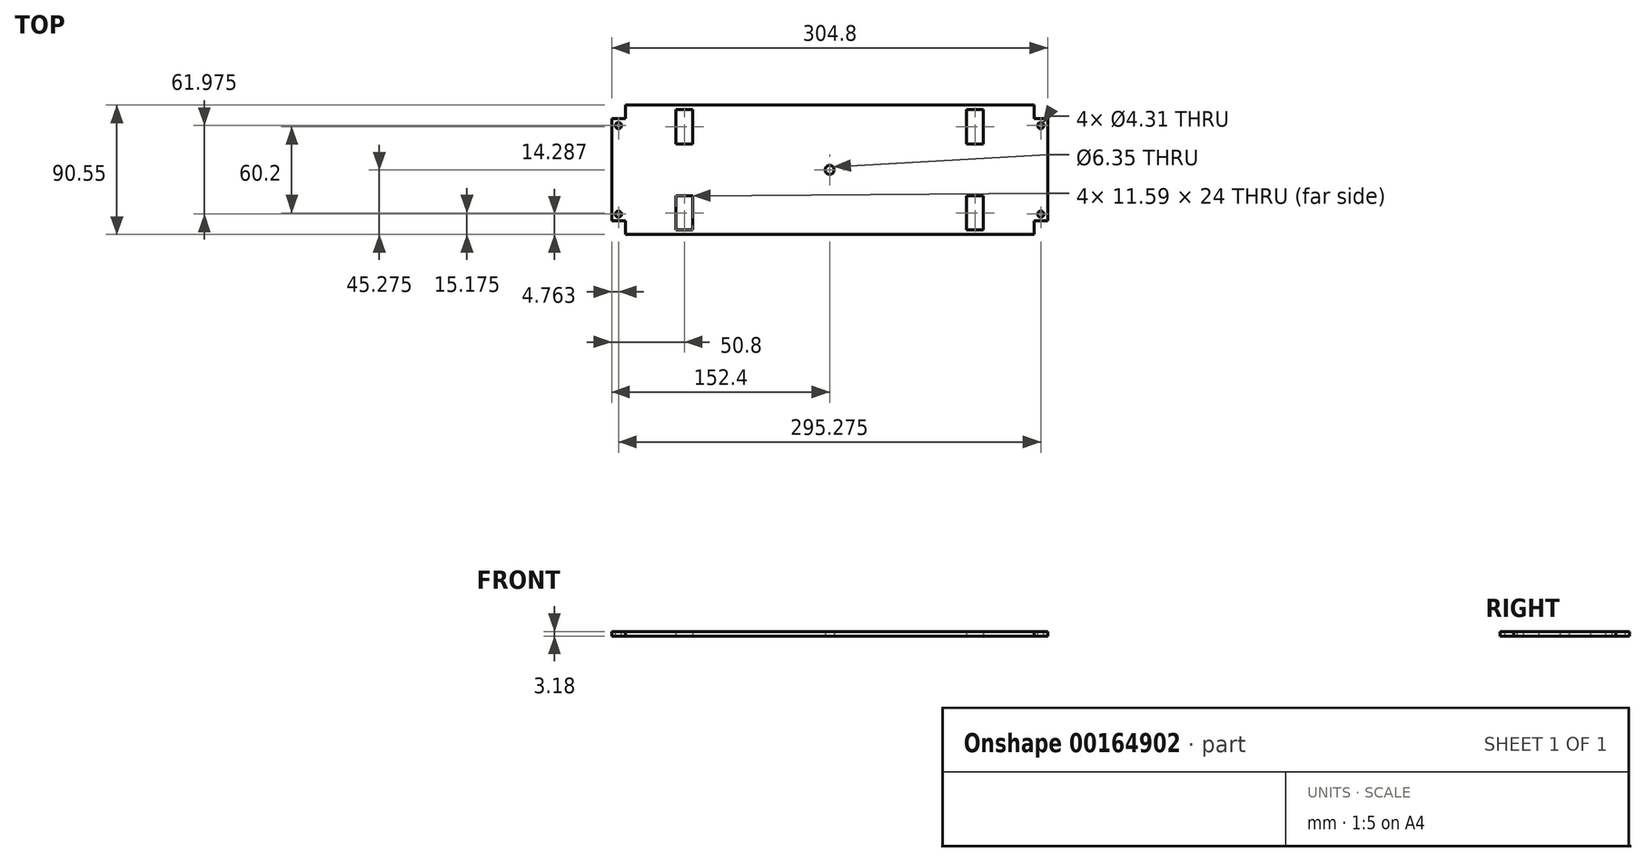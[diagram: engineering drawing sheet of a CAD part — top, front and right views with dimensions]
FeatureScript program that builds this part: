
annotation { "Feature Type Name" : "Feature", "Feature Type Description" : "" }
export const myFeature = defineFeature(function(context is Context, id is Id, definition is map)
    precondition{}
    {
        {
            var Q0;
            Q0=qCreatedBy(makeId("Top.planeOp"),FACE);
            var sketch = newSketch(context, id + "F0", { "sketchPlane" : qUnion([Q0])});
            skLineSegment(sketch, "E0.bottom", {"start": v(0, 0) * mm, "end": v(304.8, 0) * mm});
            skLineSegment(sketch, "E0.top", {"start": v(0, -90.55) * mm, "end": v(304.8, -90.55) * mm});
            skLineSegment(sketch, "E0.left", {"start": v(0, 0) * mm, "end": v(0, -90.55) * mm});
            skLineSegment(sketch, "E0.right", {"start": v(304.8, 0) * mm, "end": v(304.8, -90.55) * mm});
            skLineSegment(sketch, "E1", {"start": v(152.4, 0) * mm, "end": v(152.4, -90.55) * mm, "construction": true});
            skLineSegment(sketch, "E2.bottom", {"start": v(254, -15.18) * mm, "end": v(50.8, -15.18) * mm, "construction": true});
            skLineSegment(sketch, "E2.top", {"start": v(254, -75.38) * mm, "end": v(50.8, -75.38) * mm, "construction": true});
            skLineSegment(sketch, "E2.left", {"start": v(254, -15.18) * mm, "end": v(254, -75.38) * mm, "construction": true});
            skLineSegment(sketch, "E2.right", {"start": v(50.8, -15.18) * mm, "end": v(50.8, -75.38) * mm, "construction": true});
            skPoint(sketch, "E2.middle", {"position": v(152.4, -45.28) * mm});
            skLineSegment(sketch, "E3.bottom", {"start": v(259.8, -3.18) * mm, "end": v(248.2, -3.18) * mm});
            skLineSegment(sketch, "E3.top", {"start": v(259.8, -27.17) * mm, "end": v(248.2, -27.17) * mm});
            skLineSegment(sketch, "E3.left", {"start": v(259.8, -3.18) * mm, "end": v(259.8, -27.18) * mm});
            skLineSegment(sketch, "E3.right", {"start": v(248.2, -3.18) * mm, "end": v(248.2, -27.18) * mm});
            skPoint(sketch, "E3.middle", {"position": v(254, -15.17) * mm});
            skLineSegment(sketch, "E4.bottom", {"start": v(259.8, -87.38) * mm, "end": v(248.2, -87.38) * mm});
            skLineSegment(sketch, "E4.top", {"start": v(259.8, -63.38) * mm, "end": v(248.2, -63.38) * mm});
            skLineSegment(sketch, "E4.left", {"start": v(259.8, -87.38) * mm, "end": v(259.8, -63.38) * mm});
            skLineSegment(sketch, "E4.right", {"start": v(248.2, -87.38) * mm, "end": v(248.2, -63.38) * mm});
            skPoint(sketch, "E4.middle", {"position": v(254, -75.38) * mm});
            skLineSegment(sketch, "E5.bottom", {"start": v(45, -87.38) * mm, "end": v(56.6, -87.38) * mm});
            skLineSegment(sketch, "E5.top", {"start": v(45, -63.38) * mm, "end": v(56.6, -63.38) * mm});
            skLineSegment(sketch, "E5.left", {"start": v(45, -87.38) * mm, "end": v(45, -63.38) * mm});
            skLineSegment(sketch, "E5.right", {"start": v(56.6, -87.38) * mm, "end": v(56.6, -63.38) * mm});
            skPoint(sketch, "E5.middle", {"position": v(50.8, -75.38) * mm});
            skLineSegment(sketch, "E6.bottom", {"start": v(45, -27.18) * mm, "end": v(56.6, -27.18) * mm});
            skLineSegment(sketch, "E6.top", {"start": v(45, -3.17) * mm, "end": v(56.6, -3.17) * mm});
            skLineSegment(sketch, "E6.left", {"start": v(45, -27.18) * mm, "end": v(45, -3.18) * mm});
            skLineSegment(sketch, "E6.right", {"start": v(56.6, -27.17) * mm, "end": v(56.6, -3.18) * mm});
            skPoint(sketch, "E6.middle", {"position": v(50.8, -15.17) * mm});
            skCircle(sketch, "E7", {"center": v(152.4, -45.28) * mm, "radius": 3.18 * mm});
            skSolve(sketch);
        }
        {
            var Q0;
            Q0 = qSketchRegion(id + "F0", true);
            extrude(context, id + "F1", {"entities" : qUnion([Q0]), "depth" : 3.17 * mm});
        }
        {
            var Q0;
            Q0=makeQuery(id+"F1.opExtrude","CAP_FACE",FACE,{"disambiguationData":[OSD([sQuery(id+"F0.wireOp",EDGE,"E0.bottom"),sQuery(id+"F0.wireOp",EDGE,"E0.top"),sQuery(id+"F0.wireOp",EDGE,"E0.left"),sQuery(id+"F0.wireOp",EDGE,"E0.right"),sQuery(id+"F0.wireOp",EDGE,"E3.bottom"),sQuery(id+"F0.wireOp",EDGE,"E3.top"),sQuery(id+"F0.wireOp",EDGE,"E3.left"),sQuery(id+"F0.wireOp",EDGE,"E3.right"),sQuery(id+"F0.wireOp",EDGE,"E4.bottom"),sQuery(id+"F0.wireOp",EDGE,"E4.top"),sQuery(id+"F0.wireOp",EDGE,"E4.left"),sQuery(id+"F0.wireOp",EDGE,"E4.right"),sQuery(id+"F0.wireOp",EDGE,"E5.bottom"),sQuery(id+"F0.wireOp",EDGE,"E5.top"),sQuery(id+"F0.wireOp",EDGE,"E5.left"),sQuery(id+"F0.wireOp",EDGE,"E5.right"),sQuery(id+"F0.wireOp",EDGE,"E6.bottom"),sQuery(id+"F0.wireOp",EDGE,"E6.top"),sQuery(id+"F0.wireOp",EDGE,"E6.left"),sQuery(id+"F0.wireOp",EDGE,"E6.right")])],"isStart":false});
            var sketch = newSketch(context, id + "F2", { "sketchPlane" : qUnion([Q0])});
            skLineSegment(sketch, "E8", {"start": v(152.4, 0) * mm, "end": v(152.4, -90.55) * mm, "construction": true});
            skLineSegment(sketch, "E9.bottom", {"start": v(4.76, -14.29) * mm, "end": v(300.04, -14.29) * mm, "construction": true});
            skLineSegment(sketch, "E9.top", {"start": v(4.76, -76.26) * mm, "end": v(300.04, -76.26) * mm, "construction": true});
            skLineSegment(sketch, "E9.left", {"start": v(4.76, -14.29) * mm, "end": v(4.76, -76.26) * mm, "construction": true});
            skLineSegment(sketch, "E9.right", {"start": v(300.04, -14.29) * mm, "end": v(300.04, -76.26) * mm, "construction": true});
            skPoint(sketch, "E9.middle", {"position": v(152.4, -45.28) * mm});
            skLineSegment(sketch, "E10.bottom", {"start": v(4.76, -76.26) * mm, "end": v(0, -76.26) * mm, "construction": true});
            skLineSegment(sketch, "E10.top", {"start": v(4.76, -90.55) * mm, "end": v(0, -90.55) * mm, "construction": true});
            skLineSegment(sketch, "E10.left", {"start": v(4.76, -76.26) * mm, "end": v(4.76, -90.55) * mm, "construction": true});
            skLineSegment(sketch, "E10.right", {"start": v(0, -76.26) * mm, "end": v(0, -90.55) * mm, "construction": true});
            skCircle(sketch, "E11", {"center": v(4.76, -14.29) * mm, "radius": 2.15 * mm});
            skCircle(sketch, "E12", {"center": v(4.76, -76.26) * mm, "radius": 2.15 * mm});
            skCircle(sketch, "E13", {"center": v(300.04, -76.26) * mm, "radius": 2.15 * mm});
            skCircle(sketch, "E14", {"center": v(300.04, -14.29) * mm, "radius": 2.15 * mm});
            skSolve(sketch);
        }
        {
            var Q0;
            Q0 = qSketchRegion(id + "F2", true);
            var Q1;
            Q1=makeQuery(id+"F1.opExtrude","CAP_FACE",FACE,{"disambiguationData":[OSD([sQuery(id+"F0.wireOp",EDGE,"E0.bottom"),sQuery(id+"F0.wireOp",EDGE,"E0.top"),sQuery(id+"F0.wireOp",EDGE,"E0.left"),sQuery(id+"F0.wireOp",EDGE,"E0.right"),sQuery(id+"F0.wireOp",EDGE,"E3.bottom"),sQuery(id+"F0.wireOp",EDGE,"E3.top"),sQuery(id+"F0.wireOp",EDGE,"E3.left"),sQuery(id+"F0.wireOp",EDGE,"E3.right"),sQuery(id+"F0.wireOp",EDGE,"E4.bottom"),sQuery(id+"F0.wireOp",EDGE,"E4.top"),sQuery(id+"F0.wireOp",EDGE,"E4.left"),sQuery(id+"F0.wireOp",EDGE,"E4.right"),sQuery(id+"F0.wireOp",EDGE,"E5.bottom"),sQuery(id+"F0.wireOp",EDGE,"E5.top"),sQuery(id+"F0.wireOp",EDGE,"E5.left"),sQuery(id+"F0.wireOp",EDGE,"E5.right"),sQuery(id+"F0.wireOp",EDGE,"E6.bottom"),sQuery(id+"F0.wireOp",EDGE,"E6.top"),sQuery(id+"F0.wireOp",EDGE,"E6.left"),sQuery(id+"F0.wireOp",EDGE,"E6.right")])],"isStart":true});
            extrude(context, id + "F3", {"entities" : qUnion([Q0]), "operationType" : NewBodyOperationType.REMOVE, "endBound" : BoundingType.UP_TO_SURFACE, "oppositeDirection" : true, "endBoundEntityFace" : qUnion([Q1]), "depth" : 25.4 * mm});
        }
        {
            var Q0;
            Q0=makeQuery(id+"F1.opExtrude","CAP_FACE",FACE,{"disambiguationData":[OSD([sQuery(id+"F0.wireOp",EDGE,"E0.bottom"),sQuery(id+"F0.wireOp",EDGE,"E0.top"),sQuery(id+"F0.wireOp",EDGE,"E0.left"),sQuery(id+"F0.wireOp",EDGE,"E0.right"),sQuery(id+"F0.wireOp",EDGE,"E3.bottom"),sQuery(id+"F0.wireOp",EDGE,"E3.top"),sQuery(id+"F0.wireOp",EDGE,"E3.left"),sQuery(id+"F0.wireOp",EDGE,"E3.right"),sQuery(id+"F0.wireOp",EDGE,"E4.bottom"),sQuery(id+"F0.wireOp",EDGE,"E4.top"),sQuery(id+"F0.wireOp",EDGE,"E4.left"),sQuery(id+"F0.wireOp",EDGE,"E4.right"),sQuery(id+"F0.wireOp",EDGE,"E5.bottom"),sQuery(id+"F0.wireOp",EDGE,"E5.top"),sQuery(id+"F0.wireOp",EDGE,"E5.left"),sQuery(id+"F0.wireOp",EDGE,"E5.right"),sQuery(id+"F0.wireOp",EDGE,"E6.bottom"),sQuery(id+"F0.wireOp",EDGE,"E6.top"),sQuery(id+"F0.wireOp",EDGE,"E6.left"),sQuery(id+"F0.wireOp",EDGE,"E6.right")])],"isStart":false});
            var sketch = newSketch(context, id + "F4", { "sketchPlane" : qUnion([Q0])});
            skLineSegment(sketch, "E15.bottom", {"start": v(304.8, 0) * mm, "end": v(295.28, 0) * mm});
            skLineSegment(sketch, "E15.top", {"start": v(304.8, -9.53) * mm, "end": v(295.28, -9.53) * mm});
            skLineSegment(sketch, "E15.left", {"start": v(304.8, 0) * mm, "end": v(304.8, -9.53) * mm});
            skLineSegment(sketch, "E15.right", {"start": v(295.28, 0) * mm, "end": v(295.28, -9.53) * mm});
            skLineSegment(sketch, "E16.bottom", {"start": v(304.8, -90.55) * mm, "end": v(295.28, -90.55) * mm});
            skLineSegment(sketch, "E16.top", {"start": v(304.8, -81.03) * mm, "end": v(295.28, -81.03) * mm});
            skLineSegment(sketch, "E16.left", {"start": v(304.8, -90.55) * mm, "end": v(304.8, -81.03) * mm});
            skLineSegment(sketch, "E16.right", {"start": v(295.28, -90.55) * mm, "end": v(295.28, -81.03) * mm});
            skLineSegment(sketch, "E17.bottom", {"start": v(0, -90.55) * mm, "end": v(9.53, -90.55) * mm});
            skLineSegment(sketch, "E17.top", {"start": v(0, -81.03) * mm, "end": v(9.53, -81.03) * mm});
            skLineSegment(sketch, "E17.left", {"start": v(0, -90.55) * mm, "end": v(0, -81.03) * mm});
            skLineSegment(sketch, "E17.right", {"start": v(9.53, -90.55) * mm, "end": v(9.53, -81.03) * mm});
            skLineSegment(sketch, "E18.bottom", {"start": v(0, 0) * mm, "end": v(9.53, 0) * mm});
            skLineSegment(sketch, "E18.top", {"start": v(0, -9.53) * mm, "end": v(9.53, -9.53) * mm});
            skLineSegment(sketch, "E18.left", {"start": v(0, 0) * mm, "end": v(0, -9.53) * mm});
            skLineSegment(sketch, "E18.right", {"start": v(9.53, 0) * mm, "end": v(9.53, -9.53) * mm});
            skSolve(sketch);
        }
        {
            var Q0;
            Q0 = qSketchRegion(id + "F4", true);
            var Q1;
            Q1=makeQuery(id+"F1.opExtrude","CAP_FACE",FACE,{"disambiguationData":[OSD([sQuery(id+"F0.wireOp",EDGE,"E0.bottom"),sQuery(id+"F0.wireOp",EDGE,"E0.top"),sQuery(id+"F0.wireOp",EDGE,"E0.left"),sQuery(id+"F0.wireOp",EDGE,"E0.right"),sQuery(id+"F0.wireOp",EDGE,"E3.bottom"),sQuery(id+"F0.wireOp",EDGE,"E3.top"),sQuery(id+"F0.wireOp",EDGE,"E3.left"),sQuery(id+"F0.wireOp",EDGE,"E3.right"),sQuery(id+"F0.wireOp",EDGE,"E4.bottom"),sQuery(id+"F0.wireOp",EDGE,"E4.top"),sQuery(id+"F0.wireOp",EDGE,"E4.left"),sQuery(id+"F0.wireOp",EDGE,"E4.right"),sQuery(id+"F0.wireOp",EDGE,"E5.bottom"),sQuery(id+"F0.wireOp",EDGE,"E5.top"),sQuery(id+"F0.wireOp",EDGE,"E5.left"),sQuery(id+"F0.wireOp",EDGE,"E5.right"),sQuery(id+"F0.wireOp",EDGE,"E6.bottom"),sQuery(id+"F0.wireOp",EDGE,"E6.top"),sQuery(id+"F0.wireOp",EDGE,"E6.left"),sQuery(id+"F0.wireOp",EDGE,"E6.right")])],"isStart":true});
            extrude(context, id + "F5", {"entities" : qUnion([Q0]), "operationType" : NewBodyOperationType.REMOVE, "endBound" : BoundingType.UP_TO_SURFACE, "oppositeDirection" : true, "endBoundEntityFace" : qUnion([Q1]), "depth" : 25.4 * mm});
        }
    });
